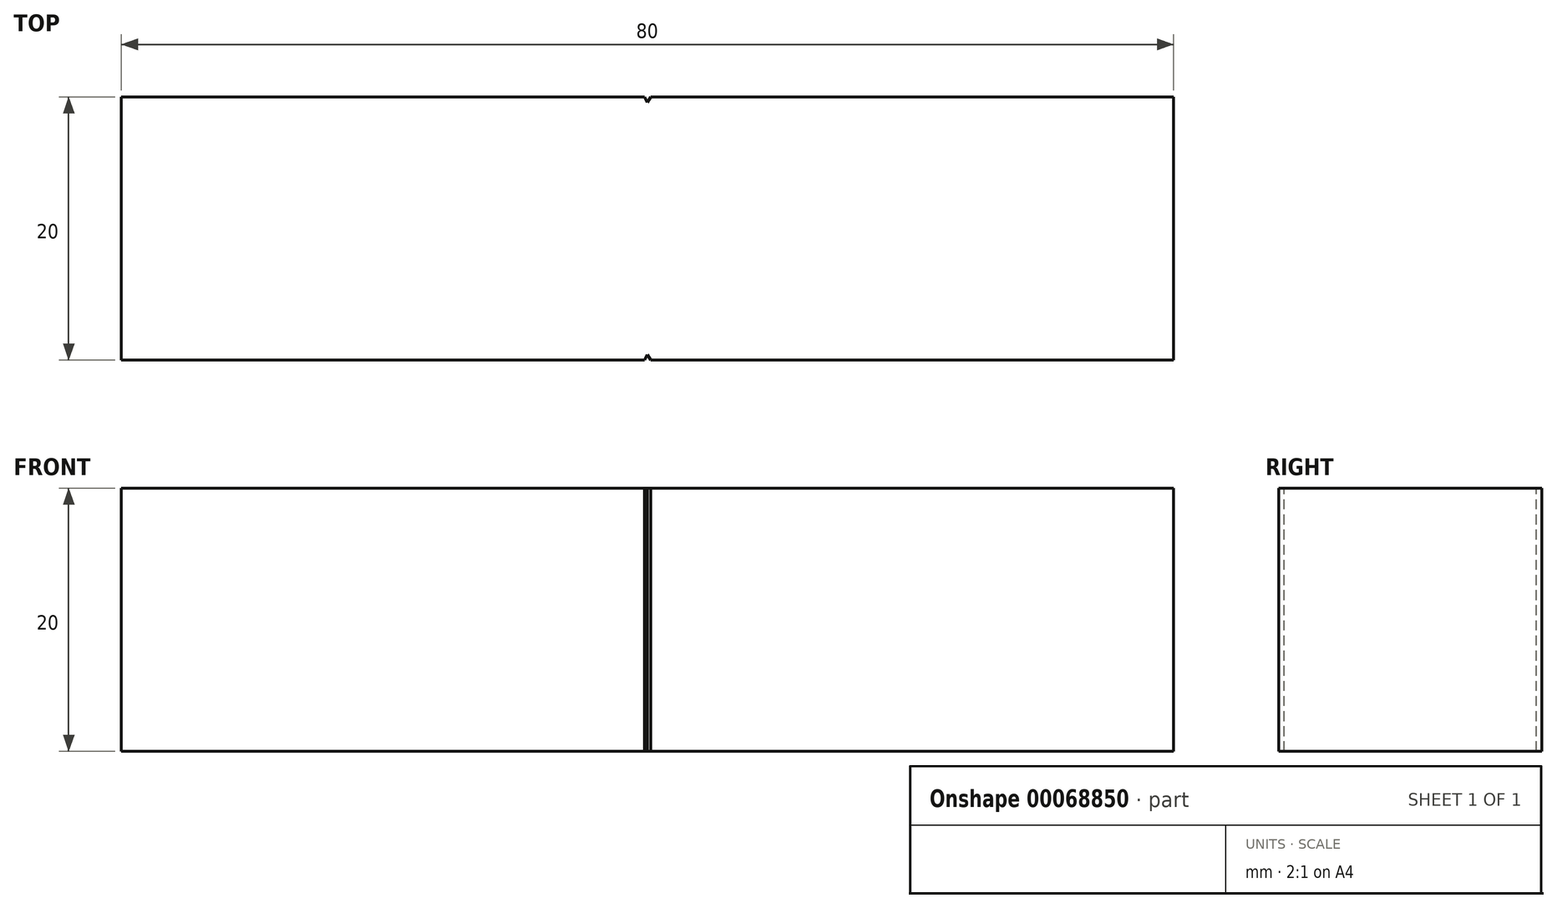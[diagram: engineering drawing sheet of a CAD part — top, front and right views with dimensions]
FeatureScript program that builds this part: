
annotation { "Feature Type Name" : "Feature", "Feature Type Description" : "" }
export const myFeature = defineFeature(function(context is Context, id is Id, definition is map)
    precondition{}
    {
        {
            var Q0;
            Q0=qCreatedBy(makeId("Top.planeOp"),FACE);
            var sketch = newSketch(context, id + "F0", { "sketchPlane" : qUnion([Q0])});
            skLineSegment(sketch, "E0.rect.bottom", {"start": v(40, -10) * mm, "end": v(-40, -10) * mm});
            skLineSegment(sketch, "E0.rect.top", {"start": v(40, 10) * mm, "end": v(-40, 10) * mm});
            skLineSegment(sketch, "E0.rect.left", {"start": v(40, -10) * mm, "end": v(40, 10) * mm});
            skLineSegment(sketch, "E0.rect.right", {"start": v(-40, -10) * mm, "end": v(-40, 10) * mm});
            skPoint(sketch, "E0.rect.middle", {"position": v(0, 0) * mm});
            skSolve(sketch);
        }
        {
            var Q0;
            Q0=makeQuery(id+"F0.imprint","IMPRINT",FACE,{"disambiguationData":[TD([[makeQuery(id+"F0.imprint","IMPRINT",EDGE,{"derivedFrom":sQuery(id+"F0.wireOp",EDGE,"E0.rect.bottom")}),-1.0]])]});
            extrude(context, id + "F1", {"entities" : qUnion([Q0]), "depth" : 20 * mm});
        }
        {
            var Q0;
            Q0=makeQuery(id+"F1.opExtrude","CAP_FACE",FACE,{"disambiguationData":[OSD([sQuery(id+"F0.wireOp",EDGE,"E0.rect.bottom"),sQuery(id+"F0.wireOp",EDGE,"E0.rect.top"),sQuery(id+"F0.wireOp",EDGE,"E0.rect.left"),sQuery(id+"F0.wireOp",EDGE,"E0.rect.right")])],"isStart":false});
            var sketch = newSketch(context, id + "F2", { "sketchPlane" : qUnion([Q0])});
            skLineSegment(sketch, "E1", {"start": v(-0.23, 10) * mm, "end": v(0, 9.6) * mm});
            skLineSegment(sketch, "E2", {"start": v(0, 9.6) * mm, "end": v(0.23, 10) * mm});
            skLineSegment(sketch, "E3", {"start": v(0.23, 10) * mm, "end": v(-0.23, 10) * mm});
            skPoint(sketch, "E4", {"position": v(0, 10) * mm});
            skPoint(sketch, "E5.MirrorP", {"position": v(0, -10) * mm});
            skLineSegment(sketch, "E6.MirrorCS", {"start": v(-0.23, -10) * mm, "end": v(0, -9.6) * mm});
            skLineSegment(sketch, "E7.MirrorCS", {"start": v(0, -9.6) * mm, "end": v(0.23, -10) * mm});
            skLineSegment(sketch, "E8.MirrorCS", {"start": v(0.23, -10) * mm, "end": v(-0.23, -10) * mm});
            skSolve(sketch);
        }
        {
            var Q0;
            Q0=makeQuery(id+"F2.imprint","IMPRINT",FACE,{"disambiguationData":[TD([[makeQuery(id+"F2.imprint","IMPRINT",EDGE,{"derivedFrom":sQuery(id+"F2.wireOp",EDGE,"E6.MirrorCS")}),-1.0]])]});
            var Q1;
            Q1=makeQuery(id+"F2.imprint","IMPRINT",FACE,{"disambiguationData":[TD([[makeQuery(id+"F2.imprint","IMPRINT",EDGE,{"derivedFrom":sQuery(id+"F2.wireOp",EDGE,"E1")}),1.0]])]});
            extrude(context, id + "F3", {"entities" : qUnion([Q0, Q1]), "operationType" : NewBodyOperationType.REMOVE, "endBound" : BoundingType.THROUGH_ALL, "oppositeDirection" : true, "depth" : 25 * mm});
        }
    });
